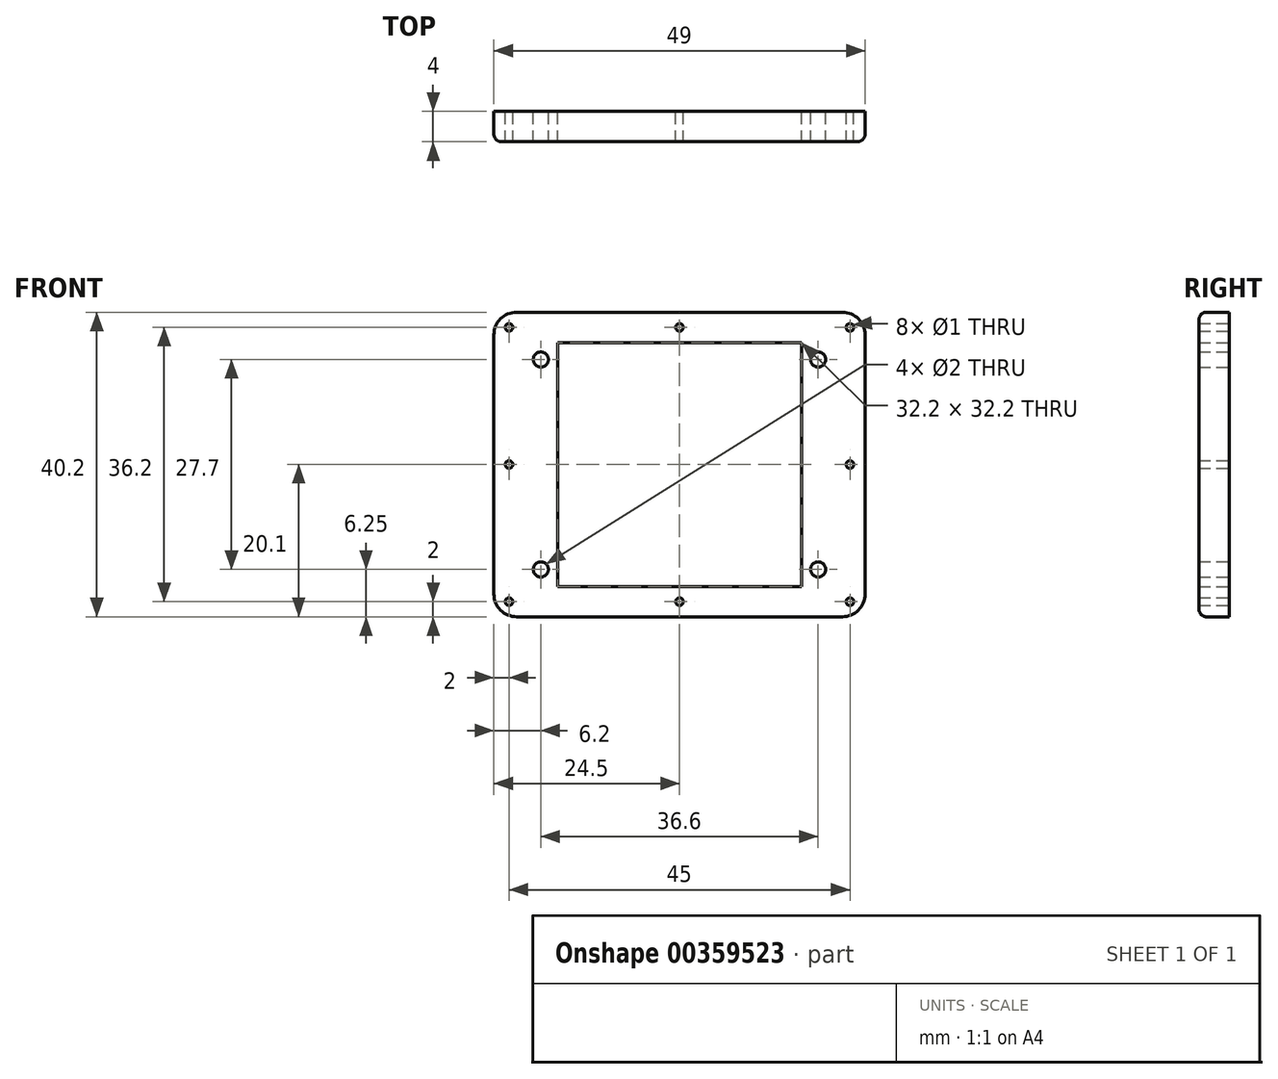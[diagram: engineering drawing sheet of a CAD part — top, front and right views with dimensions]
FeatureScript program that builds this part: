
annotation { "Feature Type Name" : "Feature", "Feature Type Description" : "" }
export const myFeature = defineFeature(function(context is Context, id is Id, definition is map)
    precondition{}
    {
        {
            var Q0;
            Q0=qCreatedBy(makeId("Front.planeOp"),FACE);
            var sketch = newSketch(context, id + "F0", { "sketchPlane" : qUnion([Q0])});
            skLineSegment(sketch, "E0.bottom", {"start": v(16.1, -16.1) * mm, "end": v(-16.1, -16.1) * mm});
            skLineSegment(sketch, "E0.top", {"start": v(16.1, 16.1) * mm, "end": v(-16.1, 16.1) * mm});
            skLineSegment(sketch, "E0.left", {"start": v(16.1, -16.1) * mm, "end": v(16.1, 16.1) * mm});
            skLineSegment(sketch, "E0.right", {"start": v(-16.1, -16.1) * mm, "end": v(-16.1, 16.1) * mm});
            skPoint(sketch, "E0.middle", {"position": v(0, 0) * mm});
            skLineSegment(sketch, "E1.bottom", {"start": v(20.5, -16.1) * mm, "end": v(-20.5, -16.1) * mm, "construction": true});
            skLineSegment(sketch, "E1.top", {"start": v(20.5, 16.1) * mm, "end": v(-20.5, 16.1) * mm, "construction": true});
            skLineSegment(sketch, "E1.left", {"start": v(20.5, -16.1) * mm, "end": v(20.5, 16.1) * mm, "construction": true});
            skLineSegment(sketch, "E1.right", {"start": v(-20.5, -16.1) * mm, "end": v(-20.5, 16.1) * mm, "construction": true});
            skCircle(sketch, "E2", {"center": v(18.3, 13.85) * mm, "radius": 1 * mm});
            skCircle(sketch, "E3.MirrorC", {"center": v(-18.3, 13.85) * mm, "radius": 1 * mm});
            skCircle(sketch, "E4.MirrorC", {"center": v(-18.3, -13.85) * mm, "radius": 1 * mm});
            skCircle(sketch, "E5.MirrorC", {"center": v(18.3, -13.85) * mm, "radius": 1 * mm});
            skLineSegment(sketch, "E6.0", {"start": v(24.5, 20.1) * mm, "end": v(-24.5, 20.1) * mm});
            skLineSegment(sketch, "E6.1", {"start": v(24.5, -20.1) * mm, "end": v(24.5, 20.1) * mm});
            skLineSegment(sketch, "E6.2", {"start": v(24.5, -20.1) * mm, "end": v(-24.5, -20.1) * mm});
            skLineSegment(sketch, "E6.3", {"start": v(-24.5, -20.1) * mm, "end": v(-24.5, 20.1) * mm});
            skLineSegment(sketch, "E7", {"start": v(0, -20.1) * mm, "end": v(0, -16.1) * mm, "construction": true});
            skLineSegment(sketch, "E8", {"start": v(-20.5, -16.1) * mm, "end": v(-24.5, -20.1) * mm, "construction": true});
            skCircle(sketch, "E9", {"center": v(0, -18.1) * mm, "radius": 0.5 * mm});
            skCircle(sketch, "E10", {"center": v(-22.5, -18.1) * mm, "radius": 0.5 * mm});
            skCircle(sketch, "E11.MirrorC", {"center": v(22.5, -18.1) * mm, "radius": 0.5 * mm});
            skCircle(sketch, "E12.MirrorC", {"center": v(22.5, 18.1) * mm, "radius": 0.5 * mm});
            skCircle(sketch, "E13.MirrorC", {"center": v(0, 18.1) * mm, "radius": 0.5 * mm});
            skCircle(sketch, "E14.MirrorC", {"center": v(-22.5, 18.1) * mm, "radius": 0.5 * mm});
            skLineSegment(sketch, "E15", {"start": v(-20.5, 0) * mm, "end": v(-24.5, 0) * mm, "construction": true});
            skCircle(sketch, "E16", {"center": v(-22.5, 0) * mm, "radius": 0.5 * mm});
            skCircle(sketch, "E17.MirrorC", {"center": v(22.5, 0) * mm, "radius": 0.5 * mm});
            skSolve(sketch);
        }
        {
            var Q0;
            Q0 = qSketchRegion(id + "F0", true);
            extrude(context, id + "F1", {"entities" : qUnion([Q0]), "depth" : 4 * mm});
        }
        {
            var Q0;
            Q0=makeQuery(id+"F1.opExtrude","SWEPT_EDGE",EDGE,{"disambiguationData":[OSD([sQuery(id+"F0.wireOp",EDGE,"E6.2"),sQuery(id+"F0.wireOp",EDGE,"E6.3")])]});
            var Q1;
            Q1=makeQuery(id+"F1.opExtrude","SWEPT_EDGE",EDGE,{"disambiguationData":[OSD([sQuery(id+"F0.wireOp",EDGE,"E6.1"),sQuery(id+"F0.wireOp",EDGE,"E6.2")])]});
            var Q2;
            Q2=makeQuery(id+"F1.opExtrude","SWEPT_EDGE",EDGE,{"disambiguationData":[OSD([sQuery(id+"F0.wireOp",EDGE,"E6.0"),sQuery(id+"F0.wireOp",EDGE,"E6.1")])]});
            var Q3;
            Q3=makeQuery(id+"F1.opExtrude","SWEPT_EDGE",EDGE,{"disambiguationData":[OSD([sQuery(id+"F0.wireOp",EDGE,"E6.0"),sQuery(id+"F0.wireOp",EDGE,"E6.3")])]});
            fillet(context, id + "F2", {"entities" : qUnion([Q0, Q1, Q2, Q3]), "radius" : 3 * mm, "tangentPropagation" : true, "allowEdgeOverflow" : false});
        }
        {
            var Q0;
            Q0=makeQuery(id+"F1.opExtrude","CAP_EDGE",EDGE,{"disambiguationData":[OSD([sQuery(id+"F0.wireOp",EDGE,"E6.0")])],"isStart":false});
            fillet(context, id + "F3", {"entities" : qUnion([Q0]), "radius" : 1 * mm, "tangentPropagation" : true, "allowEdgeOverflow" : false});
        }
    });
